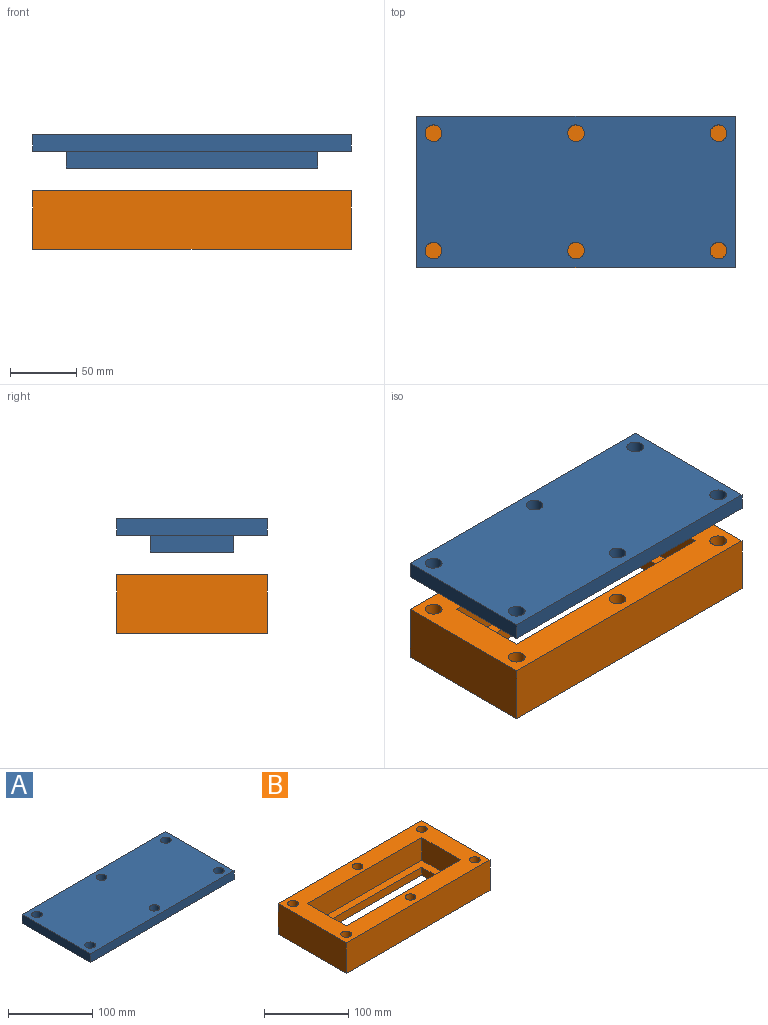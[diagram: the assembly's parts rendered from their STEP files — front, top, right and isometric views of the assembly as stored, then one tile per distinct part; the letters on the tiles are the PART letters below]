
ASSEMBLY  parts=2 mates=1
PART A: 17 faces, bbox 241.3x114.3x25.4 mm
  f0: plane 241.3x114.3mm, normal (0,0,-1), area 14723.8mm2, adj f1,f2,f3,f4,f6,f7,f8,f9
  f1: plane 241.3x12.7mm, normal (0,-1,0), area 3064.5mm2, adj f0,f2,f4,f5
  f2: plane 114.3x12.7mm, normal (1,0,0), area 1451.6mm2, adj f0,f1,f3,f5
  f3: plane 241.3x12.7mm, normal (0,1,0), area 3064.5mm2, adj f0,f2,f4,f5
  f4: plane 114.3x12.7mm, normal (-1,0,0), area 1451.6mm2, adj f0,f1,f3,f5
  f5: plane 241.3x114.3mm, normal (0,0,1), area 26820.5mm2, adj f1,f2,f3,f4,f11,f12,f13,f14
  f6: plane 63.5x12.7mm, normal (-1,0,0), area 806.5mm2, adj f0,f7,f9,f10
  f7: plane 190.5x12.7mm, normal (0,1,0), area 2419.3mm2, adj f0,f6,f8,f10
  f8: plane 63.5x12.7mm, normal (1,0,0), area 806.5mm2, adj f0,f7,f9,f10
  f9: plane 190.5x12.7mm, normal (0,-1,0), area 2419.3mm2, adj f0,f6,f8,f10
  f10: plane 190.5x63.5mm, normal (0,0,-1), area 12096.8mm2, adj f6,f7,f8,f9
  f11: cylinder r=6.35mm len=12.7mm, axis (0,0,1), area 506.7mm2, adj f0,f5
  f12: cylinder r=6.35mm len=12.7mm, axis (0,0,1), area 506.7mm2, adj f0,f5
  f13: cylinder r=6.35mm len=12.7mm, axis (0,0,1), area 506.7mm2, adj f0,f5
  f14: cylinder r=6.35mm len=12.7mm, axis (0,0,1), area 506.7mm2, adj f0,f5
  f15: cylinder r=6.35mm len=12.7mm, axis (0,0,1), area 506.7mm2, adj f0,f5
  f16: cylinder r=6.35mm len=12.7mm, axis (0,0,1), area 506.7mm2, adj f0,f5
PART B: 27 faces, bbox 241.3x114.3x44.5 mm
  f0: plane 241.3x44.45mm, normal (0,1,0), area 10725.8mm2, adj f1,f3,f4,f5
  f1: plane 114.3x44.45mm, normal (-1,0,0), area 5080.6mm2, adj f0,f2,f4,f5
  f2: plane 241.3x44.45mm, normal (0,-1,0), area 10725.8mm2, adj f1,f3,f4,f5
  f3: plane 114.3x44.45mm, normal (1,0,0), area 5080.6mm2, adj f0,f2,f4,f5
  f4: plane 241.3x114.3mm, normal (0,0,1), area 14399.6mm2, adj f0,f1,f2,f3,f6,f7,f8,f9
  f5: plane 241.3x114.3mm, normal (0,0,-1), area 19959.6mm2, adj f0,f1,f2,f3,f11,f12,f13,f14
  f6: plane 64.77x33.02mm, normal (1,0,0), area 2138.7mm2, adj f4,f7,f9,f10
  f7: plane 191.77x33.02mm, normal (0,1,0), area 6332.2mm2, adj f4,f6,f8,f10
  f8: plane 64.77x33.02mm, normal (-1,0,0), area 2138.7mm2, adj f4,f7,f9,f10
  f9: plane 191.77x33.02mm, normal (0,-1,0), area 6332.2mm2, adj f4,f6,f8,f10
  f10: plane 191.77x64.77mm, normal (0,0,1), area 4800mm2, adj f6,f7,f8,f9,f11,f12,f13,f14
  f11: plane 44.45x11.43mm, normal (1,0,0), area 508.1mm2, adj f5,f10,f12,f14
  f12: plane 171.45x11.43mm, normal (0,-1,0), area 1959.7mm2, adj f5,f10,f11,f13
  f13: plane 44.45x11.43mm, normal (-1,0,0), area 508.1mm2, adj f5,f10,f12,f14
  f14: plane 171.45x11.43mm, normal (0,1,0), area 1959.7mm2, adj f5,f10,f11,f13
  f15: cylinder r=6.35mm len=25.4mm, axis (0,0,1), area 1013.4mm2, adj f4,f16
  f16: plane 12.7x12.7mm, normal (0,0,1), area 126.7mm2, adj f15
  f17: cylinder r=6.35mm len=25.4mm, axis (0,0,1), area 1013.4mm2, adj f4,f18
  f18: plane 12.7x12.7mm, normal (0,0,1), area 126.7mm2, adj f17
  f19: cylinder r=6.35mm len=25.4mm, axis (0,0,1), area 1013.4mm2, adj f4,f20
  f20: plane 12.7x12.7mm, normal (0,0,1), area 126.7mm2, adj f19
  f21: cylinder r=6.35mm len=25.4mm, axis (0,0,1), area 1013.4mm2, adj f4,f22
  f22: plane 12.7x12.7mm, normal (0,0,1), area 126.7mm2, adj f21
  f23: cylinder r=6.35mm len=25.4mm, axis (0,0,1), area 1013.4mm2, adj f4,f24
  f24: plane 12.7x12.7mm, normal (0,0,1), area 126.7mm2, adj f23
  f25: cylinder r=6.35mm len=25.4mm, axis (0,0,1), area 1013.4mm2, adj f4,f26
  f26: plane 12.7x12.7mm, normal (0,0,1), area 126.7mm2, adj f25
PLACE A t=(-21.23,1.27,69.27)mm
PLACE B t=(-21.23,1.27,-5.11)mm fixed
MATE slider B.f21 <-> A.f15  axis (0,0,1) through (86.72,-43.18,39.34)mm
